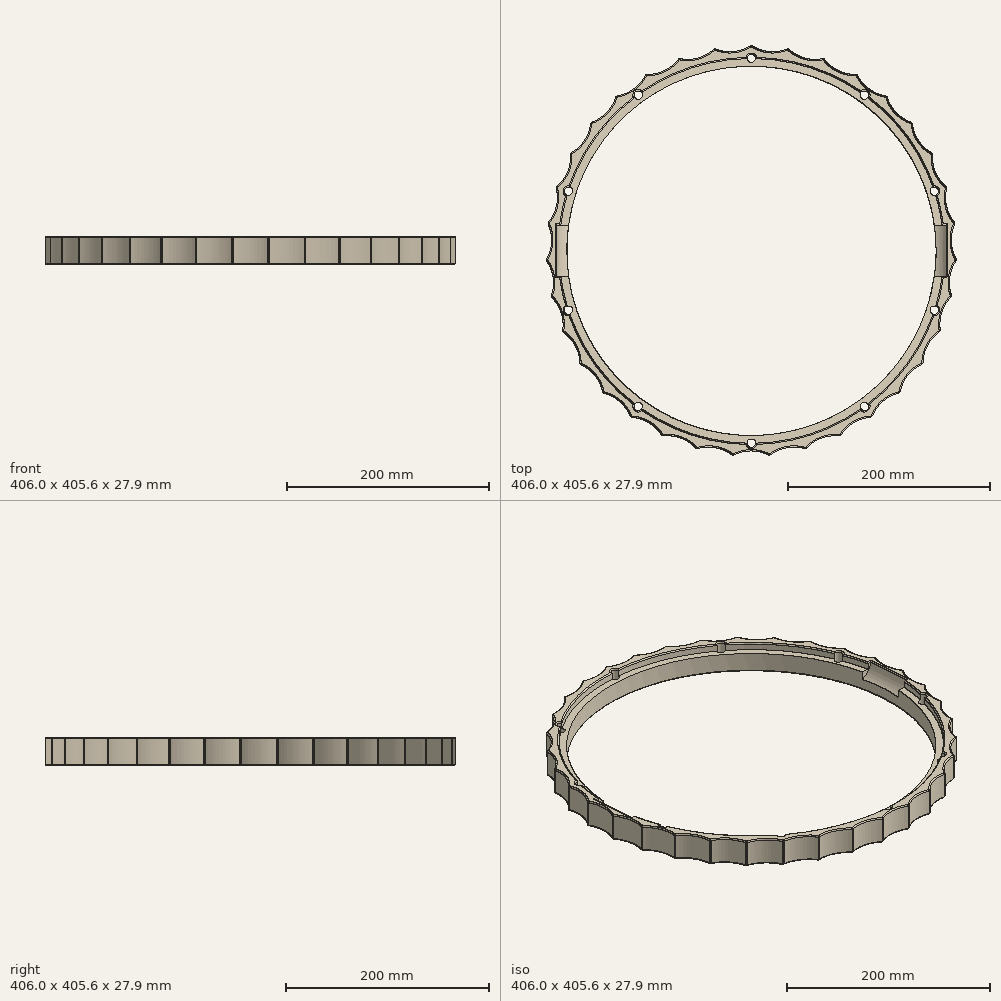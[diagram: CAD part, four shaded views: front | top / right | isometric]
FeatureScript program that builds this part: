
annotation { "Feature Type Name" : "Feature", "Feature Type Description" : "" }
export const myFeature = defineFeature(function(context is Context, id is Id, definition is map)
    precondition{}
    {
        {
            var Q0;
            Q0=qCreatedBy(makeId("Top.planeOp"),FACE);
            var sketch = newSketch(context, id + "F0", { "sketchPlane" : qUnion([Q0])});
            skCircle(sketch, "E0", {"center": v(0, 0) * mm, "radius": 182.88 * mm});
            skCircle(sketch, "E1", {"center": v(0, 0) * mm, "radius": 203.2 * mm});
            skSolve(sketch);
        }
        {
            var Q0;
            Q0=makeQuery(id+"F0.imprint","IMPRINT",FACE,{"disambiguationData":[TD([[makeQuery(id+"F0.imprint","IMPRINT",EDGE,{"derivedFrom":sQuery(id+"F0.wireOp",EDGE,"E0")}),-1.0]])]});
            extrude(context, id + "F1", {"entities" : qUnion([Q0]), "depth" : 27.94 * mm, "offsetDistance" : 25.4 * mm});
        }
        {
            var Q0;
            Q0=qCreatedBy(makeId("Top.planeOp"),FACE);
            var sketch = newSketch(context, id + "F2", { "sketchPlane" : qUnion([Q0])});
            skArc(sketch, "E2", {"start": v(-23.93, -265.87) * mm, "mid": v(0, -274.32) * mm, "end": v(23.93, -265.87) * mm});
            skArc(sketch, "E3.1.0", {"start": v(23.93, -265.87) * mm, "mid": v(48.98, -269.91) * mm, "end": v(71.02, -257.32) * mm});
            skArc(sketch, "E3.2.0", {"start": v(71.02, -257.32) * mm, "mid": v(96.39, -256.83) * mm, "end": v(115.82, -240.5) * mm});
            skArc(sketch, "E3.3.0", {"start": v(115.82, -240.5) * mm, "mid": v(140.7, -235.49) * mm, "end": v(156.9, -215.96) * mm});
            skArc(sketch, "E3.4.0", {"start": v(156.9, -215.96) * mm, "mid": v(180.49, -206.58) * mm, "end": v(192.95, -184.47) * mm});
            skArc(sketch, "E3.5.0", {"start": v(192.95, -184.47) * mm, "mid": v(214.47, -171.04) * mm, "end": v(222.78, -147.06) * mm});
            skArc(sketch, "E3.6.0", {"start": v(222.78, -147.06) * mm, "mid": v(241.56, -130) * mm, "end": v(245.46, -104.92) * mm});
            skArc(sketch, "E3.7.0", {"start": v(245.46, -104.92) * mm, "mid": v(260.9, -84.77) * mm, "end": v(260.25, -59.4) * mm});
            skArc(sketch, "E3.8.0", {"start": v(260.25, -59.4) * mm, "mid": v(271.84, -36.82) * mm, "end": v(266.67, -11.98) * mm});
            skArc(sketch, "E3.9.0", {"start": v(201.75, 27.33) * mm, "mid": v(197.92, 8.89) * mm, "end": v(203.39, -9.13) * mm});
            skArc(sketch, "E3.10.0", {"start": v(193.63, 62.91) * mm, "mid": v(193.15, 44.09) * mm, "end": v(201.75, 27.33) * mm});
            skArc(sketch, "E3.11.0", {"start": v(179.28, 96.48) * mm, "mid": v(182.18, 77.87) * mm, "end": v(193.63, 62.91) * mm});
            skArc(sketch, "E3.12.0", {"start": v(235.07, 126.5) * mm, "mid": v(228.94, 151.12) * mm, "end": v(208.7, 166.44) * mm});
            skArc(sketch, "E3.13.0", {"start": v(208.7, 166.44) * mm, "mid": v(198.28, 189.57) * mm, "end": v(175.63, 201.03) * mm});
            skArc(sketch, "E3.14.0", {"start": v(104.42, 174.78) * mm, "mid": v(116.45, 160.28) * mm, "end": v(133.95, 153.32) * mm});
            skArc(sketch, "E3.15.0", {"start": v(136.91, 229.16) * mm, "mid": v(119.02, 247.15) * mm, "end": v(93.8, 249.92) * mm});
            skArc(sketch, "E3.16.0", {"start": v(93.8, 249.92) * mm, "mid": v(72.98, 264.43) * mm, "end": v(47.66, 262.65) * mm});
            skArc(sketch, "E3.17.0", {"start": v(47.66, 262.65) * mm, "mid": v(24.59, 273.22) * mm, "end": v(0, 266.94) * mm});
            skArc(sketch, "E3.18.0", {"start": v(-36.35, 200.32) * mm, "mid": v(-17.76, 197.32) * mm, "end": v(0, 203.6) * mm});
            skArc(sketch, "E3.19.0", {"start": v(-47.66, 262.65) * mm, "mid": v(-72.98, 264.43) * mm, "end": v(-93.8, 249.92) * mm});
            skArc(sketch, "E3.20.0", {"start": v(-104.42, 174.78) * mm, "mid": v(-85.96, 178.5) * mm, "end": v(-71.54, 190.61) * mm});
            skArc(sketch, "E3.21.0", {"start": v(-136.91, 229.16) * mm, "mid": v(-161.24, 221.93) * mm, "end": v(-175.63, 201.03) * mm});
            skArc(sketch, "E3.22.0", {"start": v(-175.63, 201.03) * mm, "mid": v(-198.28, 189.57) * mm, "end": v(-208.7, 166.44) * mm});
            skArc(sketch, "E3.23.0", {"start": v(-179.28, 96.48) * mm, "mid": v(-165.35, 109.14) * mm, "end": v(-159.18, 126.94) * mm});
            skArc(sketch, "E3.24.0", {"start": v(-193.63, 62.91) * mm, "mid": v(-182.18, 77.87) * mm, "end": v(-179.28, 96.48) * mm});
            skArc(sketch, "E3.25.0", {"start": v(-201.75, 27.33) * mm, "mid": v(-193.15, 44.09) * mm, "end": v(-193.63, 62.91) * mm});
            skArc(sketch, "E3.26.0", {"start": v(-203.39, -9.13) * mm, "mid": v(-197.92, 8.89) * mm, "end": v(-201.75, 27.33) * mm});
            skArc(sketch, "E3.27.0", {"start": v(-266.67, -11.98) * mm, "mid": v(-271.84, -36.82) * mm, "end": v(-260.25, -59.4) * mm});
            skArc(sketch, "E3.28.0", {"start": v(-260.25, -59.4) * mm, "mid": v(-260.9, -84.77) * mm, "end": v(-245.46, -104.92) * mm});
            skArc(sketch, "E3.29.0", {"start": v(-245.46, -104.92) * mm, "mid": v(-241.56, -130) * mm, "end": v(-222.78, -147.06) * mm});
            skArc(sketch, "E3.30.0", {"start": v(-222.78, -147.06) * mm, "mid": v(-214.47, -171.04) * mm, "end": v(-192.95, -184.47) * mm});
            skArc(sketch, "E3.31.0", {"start": v(-192.95, -184.47) * mm, "mid": v(-180.49, -206.58) * mm, "end": v(-156.9, -215.96) * mm});
            skArc(sketch, "E3.32.0", {"start": v(-156.9, -215.96) * mm, "mid": v(-140.7, -235.49) * mm, "end": v(-115.82, -240.5) * mm});
            skArc(sketch, "E3.33.0", {"start": v(-115.82, -240.5) * mm, "mid": v(-96.39, -256.83) * mm, "end": v(-71.02, -257.32) * mm});
            skArc(sketch, "E3.34.0", {"start": v(-71.02, -257.32) * mm, "mid": v(-48.98, -269.91) * mm, "end": v(-23.93, -265.87) * mm});
            skPoint(sketch, "E3.center", {"position": v(0, 0) * mm});
            skArc(sketch, "E4.trimOffspring", {"start": v(0, 266.94) * mm, "mid": v(-24.59, 273.22) * mm, "end": v(-47.66, 262.65) * mm});
            skArc(sketch, "E5.trimOffspring", {"start": v(36.35, 200.32) * mm, "mid": v(52.7, 190.98) * mm, "end": v(71.54, 190.61) * mm});
            skArc(sketch, "E6.trimOffspring", {"start": v(0, 203.6) * mm, "mid": v(17.76, 197.32) * mm, "end": v(36.35, 200.32) * mm});
            skArc(sketch, "E7.trimOffspring", {"start": v(71.54, 190.61) * mm, "mid": v(85.96, 178.5) * mm, "end": v(104.42, 174.78) * mm});
            skArc(sketch, "E8.trimOffspring", {"start": v(-133.95, 153.32) * mm, "mid": v(-116.45, 160.28) * mm, "end": v(-104.42, 174.78) * mm});
            skArc(sketch, "E9.trimOffspring", {"start": v(-71.54, 190.61) * mm, "mid": v(-52.7, 190.98) * mm, "end": v(-36.35, 200.32) * mm});
            skArc(sketch, "E10.trimOffspring", {"start": v(-93.8, 249.92) * mm, "mid": v(-119.02, 247.15) * mm, "end": v(-136.91, 229.16) * mm});
            skArc(sketch, "E11.trimOffspring", {"start": v(253.88, 82.49) * mm, "mid": v(252.24, 107.81) * mm, "end": v(235.07, 126.5) * mm});
            skArc(sketch, "E12.trimOffspring", {"start": v(159.18, 126.94) * mm, "mid": v(165.35, 109.14) * mm, "end": v(179.28, 96.48) * mm});
            skArc(sketch, "E13.trimOffspring", {"start": v(175.63, 201.03) * mm, "mid": v(161.24, 221.93) * mm, "end": v(136.91, 229.16) * mm});
            skArc(sketch, "E14.trimOffspring", {"start": v(133.95, 153.32) * mm, "mid": v(143.2, 136.91) * mm, "end": v(159.18, 126.94) * mm});
            skArc(sketch, "E15.trimOffspring", {"start": v(-264.53, 35.83) * mm, "mid": v(-274.04, 12.3) * mm, "end": v(-266.67, -11.98) * mm});
            skArc(sketch, "E16.trimOffspring", {"start": v(-253.88, 82.49) * mm, "mid": v(-267.44, 61.04) * mm, "end": v(-264.53, 35.83) * mm});
            skArc(sketch, "E17.trimOffspring", {"start": v(-235.07, 126.5) * mm, "mid": v(-252.24, 107.81) * mm, "end": v(-253.88, 82.49) * mm});
            skArc(sketch, "E18.trimOffspring", {"start": v(-159.18, 126.94) * mm, "mid": v(-143.2, 136.91) * mm, "end": v(-133.95, 153.32) * mm});
            skArc(sketch, "E19.trimOffspring", {"start": v(-208.7, 166.44) * mm, "mid": v(-228.94, 151.12) * mm, "end": v(-235.07, 126.5) * mm});
            skArc(sketch, "E20.trimOffspring", {"start": v(-198.5, -45.3) * mm, "mid": v(-196.33, -26.6) * mm, "end": v(-203.39, -9.13) * mm});
            skArc(sketch, "E21.trimOffspring", {"start": v(-187.21, -80.02) * mm, "mid": v(-188.42, -61.22) * mm, "end": v(-198.5, -45.3) * mm});
            skArc(sketch, "E22.trimOffspring", {"start": v(-169.91, -112.16) * mm, "mid": v(-174.46, -93.88) * mm, "end": v(-187.21, -80.02) * mm});
            skArc(sketch, "E23.trimOffspring", {"start": v(-147.16, -140.7) * mm, "mid": v(-154.9, -123.53) * mm, "end": v(-169.91, -112.16) * mm});
            skArc(sketch, "E24.trimOffspring", {"start": v(-119.67, -164.71) * mm, "mid": v(-130.35, -149.2) * mm, "end": v(-147.16, -140.7) * mm});
            skArc(sketch, "E25.trimOffspring", {"start": v(-88.34, -183.43) * mm, "mid": v(-101.62, -170.08) * mm, "end": v(-119.67, -164.71) * mm});
            skArc(sketch, "E26.trimOffspring", {"start": v(-54.16, -196.26) * mm, "mid": v(-69.61, -185.49) * mm, "end": v(-88.34, -183.43) * mm});
            skArc(sketch, "E27.trimOffspring", {"start": v(-18.25, -202.78) * mm, "mid": v(-35.38, -194.94) * mm, "end": v(-54.16, -196.26) * mm});
            skArc(sketch, "E28.trimOffspring", {"start": v(18.25, -202.78) * mm, "mid": v(0, -198.12) * mm, "end": v(-18.25, -202.78) * mm});
            skArc(sketch, "E29.trimOffspring", {"start": v(54.16, -196.26) * mm, "mid": v(35.38, -194.94) * mm, "end": v(18.25, -202.78) * mm});
            skArc(sketch, "E30.trimOffspring", {"start": v(88.34, -183.43) * mm, "mid": v(69.61, -185.49) * mm, "end": v(54.16, -196.26) * mm});
            skArc(sketch, "E31.trimOffspring", {"start": v(119.67, -164.71) * mm, "mid": v(101.62, -170.08) * mm, "end": v(88.34, -183.43) * mm});
            skArc(sketch, "E32.trimOffspring", {"start": v(147.16, -140.7) * mm, "mid": v(130.35, -149.2) * mm, "end": v(119.67, -164.71) * mm});
            skArc(sketch, "E33.trimOffspring", {"start": v(169.91, -112.16) * mm, "mid": v(154.9, -123.53) * mm, "end": v(147.16, -140.7) * mm});
            skArc(sketch, "E34.trimOffspring", {"start": v(187.21, -80.02) * mm, "mid": v(174.46, -93.88) * mm, "end": v(169.91, -112.16) * mm});
            skArc(sketch, "E35.trimOffspring", {"start": v(198.5, -45.3) * mm, "mid": v(188.42, -61.22) * mm, "end": v(187.21, -80.02) * mm});
            skArc(sketch, "E36.trimOffspring", {"start": v(266.67, -11.98) * mm, "mid": v(274.04, 12.3) * mm, "end": v(264.53, 35.83) * mm});
            skArc(sketch, "E37.trimOffspring", {"start": v(203.39, -9.13) * mm, "mid": v(196.33, -26.6) * mm, "end": v(198.5, -45.3) * mm});
            skArc(sketch, "E38.trimOffspring", {"start": v(264.53, 35.83) * mm, "mid": v(267.44, 61.04) * mm, "end": v(253.88, 82.49) * mm});
            skSolve(sketch);
        }
        {
            var Q0;
            Q0=makeQuery(id+"F2.imprint","IMPRINT",FACE,{"disambiguationData":[TD([[makeQuery(id+"F2.imprint","IMPRINT",EDGE,{"derivedFrom":sQuery(id+"F2.wireOp",EDGE,"E2")}),1.0]])]});
            extrude(context, id + "F3", {"entities" : qUnion([Q0]), "operationType" : NewBodyOperationType.REMOVE, "depth" : 50.8 * mm, "offsetDistance" : 25.4 * mm});
        }
        {
            var Q0;
            Q0=qCreatedBy(makeId("Top.planeOp"),FACE);
            var sketch = newSketch(context, id + "F4", { "sketchPlane" : qUnion([Q0])});
            skPoint(sketch, "E39", {"position": v(0, 190.5) * mm});
            skPoint(sketch, "E40.1.0", {"position": v(-111.97, 154.12) * mm});
            skPoint(sketch, "E40.2.0", {"position": v(-181.18, 58.87) * mm});
            skPoint(sketch, "E40.3.0", {"position": v(-181.18, -58.87) * mm});
            skPoint(sketch, "E40.4.0", {"position": v(-111.97, -154.12) * mm});
            skPoint(sketch, "E40.5.0", {"position": v(0, -190.5) * mm});
            skPoint(sketch, "E40.6.0", {"position": v(111.97, -154.12) * mm});
            skPoint(sketch, "E40.7.0", {"position": v(181.18, -58.87) * mm});
            skPoint(sketch, "E40.8.0", {"position": v(181.18, 58.87) * mm});
            skPoint(sketch, "E40.9.0", {"position": v(111.97, 154.12) * mm});
            skPoint(sketch, "E40.center", {"position": v(0, 0) * mm});
            skSolve(sketch);
        }
        {
            var Q0;
            Q0=sQuery(id+"F4.wireOp",VERTEX,"E40.2.0");
            var Q1;
            Q1=sQuery(id+"F4.wireOp",VERTEX,"E40.3.0");
            var Q2;
            Q2=sQuery(id+"F4.wireOp",VERTEX,"E40.4.0");
            var Q3;
            Q3=sQuery(id+"F4.wireOp",VERTEX,"E40.5.0");
            var Q4;
            Q4=sQuery(id+"F4.wireOp",VERTEX,"E40.6.0");
            var Q5;
            Q5=sQuery(id+"F4.wireOp",VERTEX,"E40.7.0");
            var Q6;
            Q6=sQuery(id+"F4.wireOp",VERTEX,"E40.8.0");
            var Q7;
            Q7=sQuery(id+"F4.wireOp",VERTEX,"E40.9.0");
            var Q8;
            Q8=sQuery(id+"F4.wireOp",VERTEX,"E39");
            var Q9;
            Q9=sQuery(id+"F4.wireOp",VERTEX,"E40.1.0");
            var Q10;
            Q10=makeQuery(id+"F1.opExtrude","SWEPT_BODY",BODY,{"disambiguationData":[OSD([sQuery(id+"F0.wireOp",EDGE,"E0"),sQuery(id+"F0.wireOp",EDGE,"E1")])]});
            hole(context, id + "F5", {"style" : HoleStyle.C_BORE, "endStyle" : HoleEndStyle.BLIND, "oppositeDirection" : true, "holeDiameter" : 8.43 * mm, "cBoreDiameter" : 12.7 * mm, "cBoreDepth" : 10.16 * mm, "majorDiameter" : 25.4 * mm, "holeDepth" : 50.8 * mm, "isTappedThrough" : true, "tappedDepth" : 6.35 * mm, "tapClearance" : 3, "startFromSketch" : true, "locations" : qUnion([Q0, Q1, Q2, Q3, Q4, Q5, Q6, Q7, Q8, Q9]), "scope" : qUnion([Q10])});
        }
        {
            var Q0;
            Q0=qCreatedBy(makeId("Front.planeOp"),FACE);
            var sketch = newSketch(context, id + "F6", { "sketchPlane" : qUnion([Q0])});
            skLineSegment(sketch, "E41.bottom", {"start": v(190.5, 20.32) * mm, "end": v(165.1, 20.32) * mm});
            skLineSegment(sketch, "E41.top", {"start": v(190.5, 45.72) * mm, "end": v(165.1, 45.72) * mm});
            skLineSegment(sketch, "E41.left", {"start": v(190.5, 20.32) * mm, "end": v(190.5, 45.72) * mm});
            skLineSegment(sketch, "E41.right", {"start": v(165.1, 20.32) * mm, "end": v(165.1, 45.72) * mm});
            skLineSegment(sketch, "E42", {"start": v(0, 0) * mm, "end": v(0, -266.52) * mm, "construction": true});
            skSolve(sketch);
        }
        {
            var Q0;
            Q0=makeQuery(id+"F6.imprint","IMPRINT",FACE,{"disambiguationData":[TD([[makeQuery(id+"F6.imprint","IMPRINT",EDGE,{"derivedFrom":sQuery(id+"F6.wireOp",EDGE,"E41.bottom")}),-1.0]])]});
            var Q1;
            Q1=sQuery(id+"F6.wireOp",EDGE,"E42");
            revolve(context, id + "F7", {"operationType" : NewBodyOperationType.REMOVE, "surfaceOperationType" : NewSurfaceOperationType.NEW, "entities" : qUnion([Q0]), "axis" : qUnion([Q1]), "revolveType" : RevolveType.FULL, "oppositeDirection" : true});
        }
        {
            var Q0;
            Q0=qCreatedBy(makeId("Front.planeOp"),FACE);
            var sketch = newSketch(context, id + "F8", { "sketchPlane" : qUnion([Q0])});
            skLineSegment(sketch, "E43", {"start": v(0, 10.16) * mm, "end": v(-172.72, 10.16) * mm});
            skLineSegment(sketch, "E44", {"start": v(-193.04, 30.48) * mm, "end": v(-193.04, 35.67) * mm});
            skLineSegment(sketch, "E45", {"start": v(-193.04, 35.67) * mm, "end": v(193.04, 35.67) * mm});
            skLineSegment(sketch, "E46", {"start": v(193.04, 35.67) * mm, "end": v(193.04, 30.2) * mm});
            skLineSegment(sketch, "E47", {"start": v(172.69, 9.88) * mm, "end": v(0, 10.16) * mm});
            skPoint(sketch, "E48.visualSharp", {"position": v(-193.04, 10.16) * mm});
            skArc(sketch, "E48.filletArc", {"start": v(-193.04, 30.48) * mm, "mid": v(-187.09, 16.11) * mm, "end": v(-172.72, 10.16) * mm});
            skPoint(sketch, "E49.visualSharp", {"position": v(193.04, 9.85) * mm});
            skArc(sketch, "E49.filletArc", {"start": v(172.69, 9.88) * mm, "mid": v(187.08, 15.82) * mm, "end": v(193.04, 30.2) * mm});
            skSolve(sketch);
        }
        {
            var Q0;
            Q0=makeQuery(id+"F8.imprint","IMPRINT",FACE,{"disambiguationData":[TD([[makeQuery(id+"F8.imprint","IMPRINT",EDGE,{"derivedFrom":sQuery(id+"F8.wireOp",EDGE,"E43")}),-1.0]])]});
            extrude(context, id + "F9", {"entities" : qUnion([Q0]), "operationType" : NewBodyOperationType.REMOVE, "oppositeDirection" : true, "depth" : 50.8 * mm, "offsetDistance" : 25.4 * mm, "symmetric" : true});
        }
        {
            var Q0;
            Q0=makeQuery(id+"F3.boolean.opBoolean","INTERSECT",EDGE,{"derivedFrom":[makeQuery(id+"F1.opExtrude","CAP_FACE",FACE,{"disambiguationData":[OSD([sQuery(id+"F0.wireOp",EDGE,"E0"),sQuery(id+"F0.wireOp",EDGE,"E1")])],"isStart":false}),makeQuery(id+"F3.opExtrude","SWEPT_FACE",FACE,{"disambiguationData":[OSD([sQuery(id+"F2.wireOp",EDGE,"E24.trimOffspring")])]})]});
            var Q1;
            Q1=makeQuery(id+"F3.boolean.opBoolean","INTERSECT",EDGE,{"derivedFrom":[makeQuery(id+"F1.opExtrude","CAP_FACE",FACE,{"disambiguationData":[OSD([sQuery(id+"F0.wireOp",EDGE,"E0"),sQuery(id+"F0.wireOp",EDGE,"E1")])],"isStart":false}),makeQuery(id+"F3.opExtrude","SWEPT_FACE",FACE,{"disambiguationData":[OSD([sQuery(id+"F2.wireOp",EDGE,"E23.trimOffspring")])]})]});
            var Q2;
            Q2=makeQuery(id+"F3.boolean.opBoolean","INTERSECT",EDGE,{"disambiguationData":[OD(0.0)],"derivedFrom":[makeQuery(id+"F1.opExtrude","SWEPT_FACE",FACE,{"disambiguationData":[OSD([sQuery(id+"F0.wireOp",EDGE,"E1")])]}),makeQuery(id+"F3.opExtrude","SWEPT_FACE",FACE,{"disambiguationData":[OSD([sQuery(id+"F2.wireOp",EDGE,"E24.trimOffspring")])]})]});
            var Q3;
            Q3=makeQuery(id+"F3.boolean.opBoolean","INTERSECT",EDGE,{"disambiguationData":[OD(1.0)],"derivedFrom":[makeQuery(id+"F1.opExtrude","SWEPT_FACE",FACE,{"disambiguationData":[OSD([sQuery(id+"F0.wireOp",EDGE,"E1")])]}),makeQuery(id+"F3.opExtrude","SWEPT_FACE",FACE,{"disambiguationData":[OSD([sQuery(id+"F2.wireOp",EDGE,"E23.trimOffspring")])]})]});
            var Q4;
            Q4=makeQuery(id+"F3.boolean.opBoolean","INTERSECT",EDGE,{"derivedFrom":[makeQuery(id+"F1.opExtrude","CAP_FACE",FACE,{"disambiguationData":[OSD([sQuery(id+"F0.wireOp",EDGE,"E0"),sQuery(id+"F0.wireOp",EDGE,"E1")])],"isStart":false}),makeQuery(id+"F3.opExtrude","SWEPT_FACE",FACE,{"disambiguationData":[OSD([sQuery(id+"F2.wireOp",EDGE,"E25.trimOffspring")])]})]});
            var Q5;
            Q5=makeQuery(id+"F3.boolean.opBoolean","INTERSECT",EDGE,{"disambiguationData":[OD(0.0)],"derivedFrom":[makeQuery(id+"F1.opExtrude","SWEPT_FACE",FACE,{"disambiguationData":[OSD([sQuery(id+"F0.wireOp",EDGE,"E1")])]}),makeQuery(id+"F3.opExtrude","SWEPT_FACE",FACE,{"disambiguationData":[OSD([sQuery(id+"F2.wireOp",EDGE,"E25.trimOffspring")])]})]});
            var Q6;
            Q6=makeQuery(id+"F3.boolean.opBoolean","INTERSECT",EDGE,{"disambiguationData":[OD(1.0)],"derivedFrom":[makeQuery(id+"F1.opExtrude","SWEPT_FACE",FACE,{"disambiguationData":[OSD([sQuery(id+"F0.wireOp",EDGE,"E1")])]}),makeQuery(id+"F3.opExtrude","SWEPT_FACE",FACE,{"disambiguationData":[OSD([sQuery(id+"F2.wireOp",EDGE,"E24.trimOffspring")])]})]});
            var Q7;
            Q7=makeQuery(id+"F3.boolean.opBoolean","INTERSECT",EDGE,{"disambiguationData":[OD(0.0)],"derivedFrom":[makeQuery(id+"F1.opExtrude","SWEPT_FACE",FACE,{"disambiguationData":[OSD([sQuery(id+"F0.wireOp",EDGE,"E1")])]}),makeQuery(id+"F3.opExtrude","SWEPT_FACE",FACE,{"disambiguationData":[OSD([sQuery(id+"F2.wireOp",EDGE,"E26.trimOffspring")])]})]});
            var Q8;
            Q8=makeQuery(id+"F3.boolean.opBoolean","INTERSECT",EDGE,{"disambiguationData":[OD(1.0)],"derivedFrom":[makeQuery(id+"F1.opExtrude","SWEPT_FACE",FACE,{"disambiguationData":[OSD([sQuery(id+"F0.wireOp",EDGE,"E1")])]}),makeQuery(id+"F3.opExtrude","SWEPT_FACE",FACE,{"disambiguationData":[OSD([sQuery(id+"F2.wireOp",EDGE,"E25.trimOffspring")])]})]});
            var Q9;
            Q9=makeQuery(id+"F1.opExtrude","CAP_FACE",FACE,{"disambiguationData":[OSD([sQuery(id+"F0.wireOp",EDGE,"E0"),sQuery(id+"F0.wireOp",EDGE,"E1")])],"isStart":false});
            var Q10;
            Q10=makeQuery(id+"F1.opExtrude","CAP_FACE",FACE,{"disambiguationData":[OSD([sQuery(id+"F0.wireOp",EDGE,"E0"),sQuery(id+"F0.wireOp",EDGE,"E1")])],"isStart":true});
            var Q11;
            Q11=makeQuery(id+"F3.boolean.opBoolean","COPY",FACE,{"derivedFrom":makeQuery(id+"F3.opExtrude","SWEPT_FACE",FACE,{"disambiguationData":[OSD([sQuery(id+"F2.wireOp",EDGE,"E22.trimOffspring")])]})});
            var Q12;
            Q12=makeQuery(id+"F3.boolean.opBoolean","COPY",FACE,{"derivedFrom":makeQuery(id+"F3.opExtrude","SWEPT_FACE",FACE,{"disambiguationData":[OSD([sQuery(id+"F2.wireOp",EDGE,"E23.trimOffspring")])]})});
            var Q13;
            Q13=makeQuery(id+"F3.boolean.opBoolean","COPY",FACE,{"derivedFrom":makeQuery(id+"F3.opExtrude","SWEPT_FACE",FACE,{"disambiguationData":[OSD([sQuery(id+"F2.wireOp",EDGE,"E20.trimOffspring")])]})});
            var Q14;
            Q14=makeQuery(id+"F3.boolean.opBoolean","COPY",FACE,{"derivedFrom":makeQuery(id+"F3.opExtrude","SWEPT_FACE",FACE,{"disambiguationData":[OSD([sQuery(id+"F2.wireOp",EDGE,"E21.trimOffspring")])]})});
            var Q15;
            Q15=makeQuery(id+"F3.boolean.opBoolean","COPY",FACE,{"derivedFrom":makeQuery(id+"F3.opExtrude","SWEPT_FACE",FACE,{"disambiguationData":[OSD([sQuery(id+"F2.wireOp",EDGE,"E3.26.0")])]})});
            var Q16;
            Q16=makeQuery(id+"F3.boolean.opBoolean","COPY",FACE,{"derivedFrom":makeQuery(id+"F3.opExtrude","SWEPT_FACE",FACE,{"disambiguationData":[OSD([sQuery(id+"F2.wireOp",EDGE,"E3.25.0")])]})});
            var Q17;
            Q17=makeQuery(id+"F3.boolean.opBoolean","COPY",FACE,{"derivedFrom":makeQuery(id+"F3.opExtrude","SWEPT_FACE",FACE,{"disambiguationData":[OSD([sQuery(id+"F2.wireOp",EDGE,"E3.24.0")])]})});
            var Q18;
            Q18=makeQuery(id+"F3.boolean.opBoolean","COPY",FACE,{"derivedFrom":makeQuery(id+"F3.opExtrude","SWEPT_FACE",FACE,{"disambiguationData":[OSD([sQuery(id+"F2.wireOp",EDGE,"E3.23.0")])]})});
            var Q19;
            Q19=makeQuery(id+"F3.boolean.opBoolean","COPY",FACE,{"derivedFrom":makeQuery(id+"F3.opExtrude","SWEPT_FACE",FACE,{"disambiguationData":[OSD([sQuery(id+"F2.wireOp",EDGE,"E18.trimOffspring")])]})});
            var Q20;
            Q20=makeQuery(id+"F3.boolean.opBoolean","COPY",FACE,{"derivedFrom":makeQuery(id+"F3.opExtrude","SWEPT_FACE",FACE,{"disambiguationData":[OSD([sQuery(id+"F2.wireOp",EDGE,"E8.trimOffspring")])]})});
            var Q21;
            Q21=makeQuery(id+"F3.boolean.opBoolean","COPY",FACE,{"derivedFrom":makeQuery(id+"F3.opExtrude","SWEPT_FACE",FACE,{"disambiguationData":[OSD([sQuery(id+"F2.wireOp",EDGE,"E3.20.0")])]})});
            var Q22;
            Q22=makeQuery(id+"F3.boolean.opBoolean","COPY",FACE,{"derivedFrom":makeQuery(id+"F3.opExtrude","SWEPT_FACE",FACE,{"disambiguationData":[OSD([sQuery(id+"F2.wireOp",EDGE,"E9.trimOffspring")])]})});
            var Q23;
            Q23=makeQuery(id+"F3.boolean.opBoolean","COPY",FACE,{"derivedFrom":makeQuery(id+"F3.opExtrude","SWEPT_FACE",FACE,{"disambiguationData":[OSD([sQuery(id+"F2.wireOp",EDGE,"E3.18.0")])]})});
            var Q24;
            Q24=makeQuery(id+"F3.boolean.opBoolean","COPY",FACE,{"derivedFrom":makeQuery(id+"F3.opExtrude","SWEPT_FACE",FACE,{"disambiguationData":[OSD([sQuery(id+"F2.wireOp",EDGE,"E6.trimOffspring")])]})});
            var Q25;
            Q25=makeQuery(id+"F3.boolean.opBoolean","COPY",FACE,{"derivedFrom":makeQuery(id+"F3.opExtrude","SWEPT_FACE",FACE,{"disambiguationData":[OSD([sQuery(id+"F2.wireOp",EDGE,"E3.11.0")])]})});
            var Q26;
            Q26=makeQuery(id+"F3.boolean.opBoolean","COPY",FACE,{"derivedFrom":makeQuery(id+"F3.opExtrude","SWEPT_FACE",FACE,{"disambiguationData":[OSD([sQuery(id+"F2.wireOp",EDGE,"E12.trimOffspring")])]})});
            var Q27;
            Q27=makeQuery(id+"F3.boolean.opBoolean","COPY",FACE,{"derivedFrom":makeQuery(id+"F3.opExtrude","SWEPT_FACE",FACE,{"disambiguationData":[OSD([sQuery(id+"F2.wireOp",EDGE,"E14.trimOffspring")])]})});
            var Q28;
            Q28=makeQuery(id+"F3.boolean.opBoolean","COPY",FACE,{"derivedFrom":makeQuery(id+"F3.opExtrude","SWEPT_FACE",FACE,{"disambiguationData":[OSD([sQuery(id+"F2.wireOp",EDGE,"E3.14.0")])]})});
            var Q29;
            Q29=makeQuery(id+"F3.boolean.opBoolean","COPY",FACE,{"derivedFrom":makeQuery(id+"F3.opExtrude","SWEPT_FACE",FACE,{"disambiguationData":[OSD([sQuery(id+"F2.wireOp",EDGE,"E7.trimOffspring")])]})});
            var Q30;
            Q30=makeQuery(id+"F3.boolean.opBoolean","COPY",FACE,{"derivedFrom":makeQuery(id+"F3.opExtrude","SWEPT_FACE",FACE,{"disambiguationData":[OSD([sQuery(id+"F2.wireOp",EDGE,"E5.trimOffspring")])]})});
            var Q31;
            Q31=makeQuery(id+"F3.boolean.opBoolean","COPY",FACE,{"derivedFrom":makeQuery(id+"F3.opExtrude","SWEPT_FACE",FACE,{"disambiguationData":[OSD([sQuery(id+"F2.wireOp",EDGE,"E3.10.0")])]})});
            var Q32;
            Q32=makeQuery(id+"F3.boolean.opBoolean","COPY",FACE,{"derivedFrom":makeQuery(id+"F3.opExtrude","SWEPT_FACE",FACE,{"disambiguationData":[OSD([sQuery(id+"F2.wireOp",EDGE,"E3.9.0")])]})});
            var Q33;
            Q33=makeQuery(id+"F3.boolean.opBoolean","COPY",FACE,{"derivedFrom":makeQuery(id+"F3.opExtrude","SWEPT_FACE",FACE,{"disambiguationData":[OSD([sQuery(id+"F2.wireOp",EDGE,"E37.trimOffspring")])]})});
            var Q34;
            Q34=makeQuery(id+"F3.boolean.opBoolean","COPY",FACE,{"derivedFrom":makeQuery(id+"F3.opExtrude","SWEPT_FACE",FACE,{"disambiguationData":[OSD([sQuery(id+"F2.wireOp",EDGE,"E35.trimOffspring")])]})});
            var Q35;
            Q35=makeQuery(id+"F3.boolean.opBoolean","COPY",FACE,{"derivedFrom":makeQuery(id+"F3.opExtrude","SWEPT_FACE",FACE,{"disambiguationData":[OSD([sQuery(id+"F2.wireOp",EDGE,"E34.trimOffspring")])]})});
            var Q36;
            Q36=makeQuery(id+"F3.boolean.opBoolean","COPY",FACE,{"derivedFrom":makeQuery(id+"F3.opExtrude","SWEPT_FACE",FACE,{"disambiguationData":[OSD([sQuery(id+"F2.wireOp",EDGE,"E33.trimOffspring")])]})});
            var Q37;
            Q37=makeQuery(id+"F3.boolean.opBoolean","COPY",FACE,{"derivedFrom":makeQuery(id+"F3.opExtrude","SWEPT_FACE",FACE,{"disambiguationData":[OSD([sQuery(id+"F2.wireOp",EDGE,"E32.trimOffspring")])]})});
            var Q38;
            Q38=makeQuery(id+"F3.boolean.opBoolean","COPY",FACE,{"derivedFrom":makeQuery(id+"F3.opExtrude","SWEPT_FACE",FACE,{"disambiguationData":[OSD([sQuery(id+"F2.wireOp",EDGE,"E31.trimOffspring")])]})});
            var Q39;
            Q39=makeQuery(id+"F3.boolean.opBoolean","COPY",FACE,{"derivedFrom":makeQuery(id+"F3.opExtrude","SWEPT_FACE",FACE,{"disambiguationData":[OSD([sQuery(id+"F2.wireOp",EDGE,"E30.trimOffspring")])]})});
            var Q40;
            Q40=makeQuery(id+"F3.boolean.opBoolean","COPY",FACE,{"derivedFrom":makeQuery(id+"F3.opExtrude","SWEPT_FACE",FACE,{"disambiguationData":[OSD([sQuery(id+"F2.wireOp",EDGE,"E29.trimOffspring")])]})});
            var Q41;
            Q41=makeQuery(id+"F3.boolean.opBoolean","COPY",FACE,{"derivedFrom":makeQuery(id+"F3.opExtrude","SWEPT_FACE",FACE,{"disambiguationData":[OSD([sQuery(id+"F2.wireOp",EDGE,"E28.trimOffspring")])]})});
            fillet(context, id + "F10", {"entities" : qUnion([Q0, Q1, Q2, Q3, Q4, Q5, Q6, Q7, Q8, Q9, Q10, Q11, Q12, Q13, Q14, Q15, Q16, Q17, Q18, Q19, Q20, Q21, Q22, Q23, Q24, Q25, Q26, Q27, Q28, Q29, Q30, Q31, Q32, Q33, Q34, Q35, Q36, Q37, Q38, Q39, Q40, Q41]), "tangentPropagation" : true, "radius" : 1.27 * mm, "defaultsChanged" : false, "vertexSettings" : [], "allowEdgeOverflow" : false});
        }
    });
